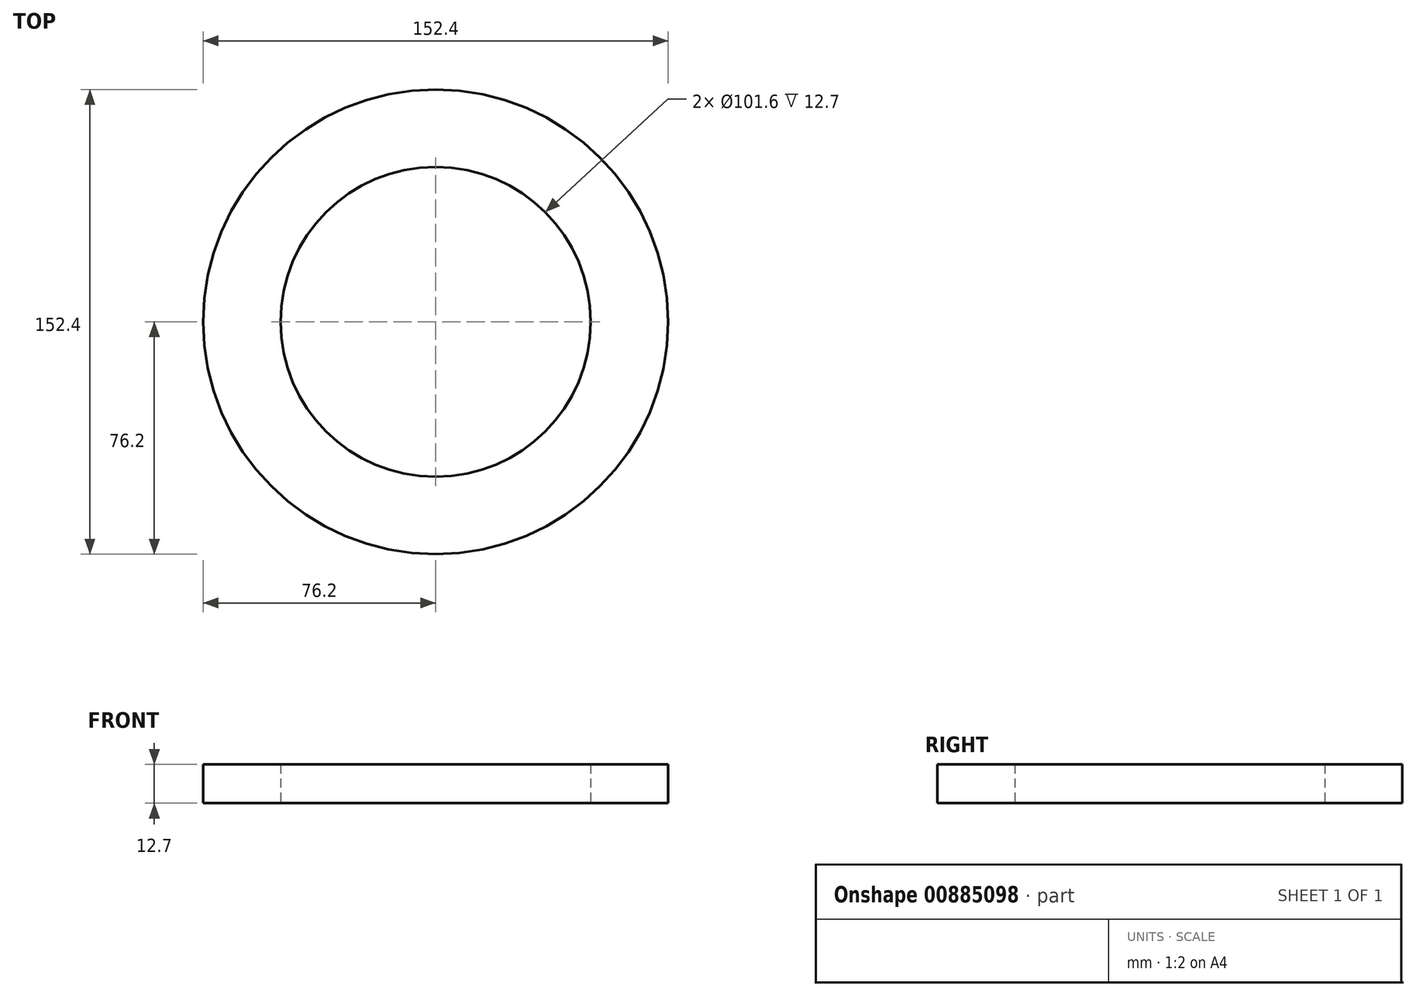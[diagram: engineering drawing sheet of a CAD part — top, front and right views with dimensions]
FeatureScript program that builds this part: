
annotation { "Feature Type Name" : "Feature", "Feature Type Description" : "" }
export const myFeature = defineFeature(function(context is Context, id is Id, definition is map)
    precondition{}
    {
        {
            var Q0;
            Q0=qCreatedBy(makeId("Top.planeOp"),FACE);
            var sketch = newSketch(context, id + "F0", { "sketchPlane" : qUnion([Q0])});
            skCircle(sketch, "E0", {"center": v(0, 0) * mm, "radius": 76.2 * mm});
            skCircle(sketch, "E1", {"center": v(0, 0) * mm, "radius": 50.8 * mm});
            skSolve(sketch);
        }
        {
            var Q0;
            Q0=makeQuery(id+"F0.imprint","IMPRINT",FACE,{"disambiguationData":[TD([[makeQuery(id+"F0.imprint","IMPRINT",EDGE,{"derivedFrom":sQuery(id+"F0.wireOp",EDGE,"E0")}),1.0]])]});
            extrude(context, id + "F1", {"entities" : qUnion([Q0]), "depth" : 12.7 * mm, "offsetDistance" : 25.4 * mm});
        }
    });
